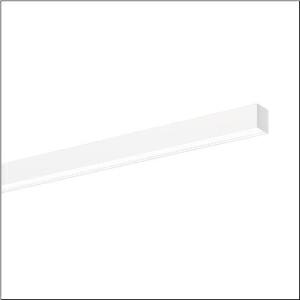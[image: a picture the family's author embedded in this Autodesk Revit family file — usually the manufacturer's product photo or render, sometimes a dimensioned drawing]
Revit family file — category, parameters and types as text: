
# Revit family: silica_r__21_51mx23dc4awb_8ea6
name_source: partatom
category: Lighting Fixtures
units: mm (PartAtom-declared; Revit-internal decimal feet)

## family parameters
Cut with Voids When Loaded = No
Host = Face
Light Source = No
Part Type = Normal
Room Calculation Point = No
Round Connector Dimension = Use Diameter
Shared = No

## types (1)
- --- (1 x LED, 8200 lm, 58.2 W, 4000K)
    Apparent Load = 58 VA
    CIE Flux Codes = 78 96 99 100 100
    Color Rendering = 80
    Color Temperature = 4000K
    Default Elevation = 1800 mm
    Description = Silica® 21, office luminaire, primary optical cover: prismatic diffuser, of PMMA, CAT 2 (L<= 3000cd/m²), light emission: direct distribution, primary light characteristic: symmetric, installation type: surface-mounted, LED, rated luminous flux: 8.200lm, luminous efficacy: 141lm/W, light colour: 840, colour temperature: 4000K, with terminal, 3+2-pole, max. 2.5mm², mains connection: 220..240V, AC, 50/60Hz, rated input power: 58.2W, luminaire housing, of aluminium, traffic white (RAL 9016), length: 3.004mm, width: 53mm, height: 53mm, protection rating (complete): IP20, insulation class (complete): insulation class I (protective earthing), certification: CE, permissible operating ambient temperature: 0..+35°C, standard: EN 50419, packaging unit: 1 piece
    Height = 0 mm  [stored 0 ft]
    Lamp = 1 x LED
    Lamp Light Flux = 8200 lm
    Lamp Power = 58.2 W
    Lamp count = 1
    Length = 3004 mm
    Luminous efficacy = 141 lm/W
    Manufacturer = Siteco
    ModVariant = No
    Model = 51MX23DC4AWB
    Mounting Place = Ceiling
    Mounting Type = Recessed
    Number of Poles = 1
    OnlyDefault = Yes
    Power Factor = 1
    Product Name = Silica® 21
    Product group = office luminaire | ceiling recessed
    ProductGroupID = 400
    Protection Class = Protection class I
    Protection Degree = IP 20
    RLX_Detail_Level = 1
    RLX_Emergency_Light_Flux = 0 lm
    RLX_Emergency_Type = 0
    RLX_Emergency_Type_DB = No
    RlxData = <blob elided: 18665 chars, md5=077d4935>
    Socket = socket
    Standby Power = 0 W
    System Light Flux = 8200 lm
    System Power = 58 W
    Type Comments = factory setting: luminous flux: 100 % | dim-lin: 254 | 323 mA
    Type Image = l_1335877.jpg
    URL = http://relux.com
    VarID = @adj_088925
    Voltage = 0 V
    Weight = 0.00 kg
    Width = 53 mm

note: [stored X ft] marks values corroborated as IEEE doubles in the binary element streams (Revit-internal decimal feet)

## geometry (parser evidence)
native form markers: Blend x4, Sweep x10
no freeform markers — native parametric forms only
